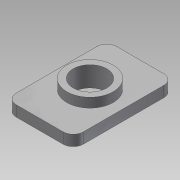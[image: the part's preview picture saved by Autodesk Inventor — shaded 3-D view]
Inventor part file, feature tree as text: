
AUTODESK INVENTOR PART (.ipt)
format: ipt  version: 2013 SP2 (Build 170200200, 200)  size: 98,816 bytes
history: native  units: mm
features: sketch x3, extrude x2, hole x1, fillet x1
ambient origin geometry x8: Origin, YZ Plane, XZ Plane, XY Plane, X Axis, Y Axis, Z Axis, Center Point
bodies: Solid1 (feature_tree)
feature tree (7):
  extrude  "Extrusion1"  Depth=15.0mm
  extrude  "Extrusion2"  Depth=6.9mm
  hole  "Hole1"  [1 undecoded]
  fillet  "Fillet1"  [1 undecoded]
  sketch  "Sketch1"  dims[d0=10.0mm d1=15.0mm]
  sketch  "Sketch2"  dims[d2=1.6mm d3=0.0mm d4=6.9mm]
  sketch  "Sketch3"  dims[d5=1.4mm d6=0.0mm d7=5.0mm d8=6.0mm d9=4.0mm d10=2.0mm d11=90.0deg d12=8.0mm d13=20.594885mm d14=1.5mm]
note: 2 required parameter values undecoded (feature->parameter linkage not recoverable at this tier; creation-order binding heuristic only, values carry confidence <= 0.55)
